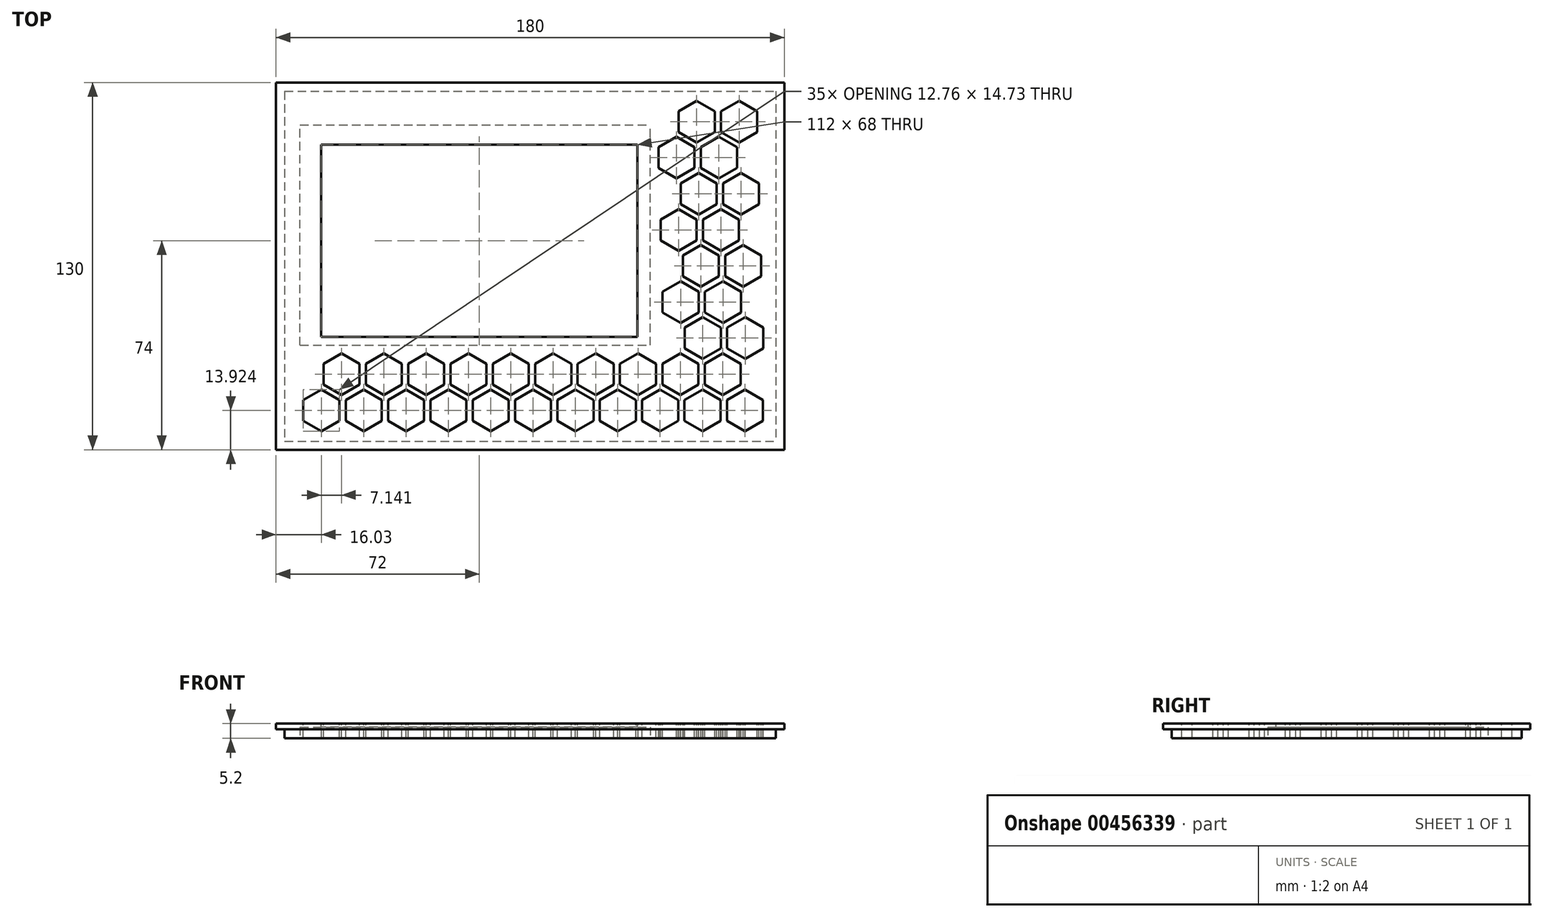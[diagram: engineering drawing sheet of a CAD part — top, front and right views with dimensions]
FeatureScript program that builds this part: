
annotation { "Feature Type Name" : "Feature", "Feature Type Description" : "" }
export const myFeature = defineFeature(function(context is Context, id is Id, definition is map)
    precondition{}
    {
        {
            var Q0;
            Q0=qCreatedBy(makeId("Top.planeOp"),FACE);
            var sketch = newSketch(context, id + "F0", { "sketchPlane" : qUnion([Q0])});
            skLineSegment(sketch, "E0.bottom", {"start": v(42.5, 28) * mm, "end": v(-42.5, 28) * mm});
            skLineSegment(sketch, "E0.top", {"start": v(42.5, -28) * mm, "end": v(-42.5, -28) * mm});
            skLineSegment(sketch, "E0.left", {"start": v(42.5, 28) * mm, "end": v(42.5, -28) * mm});
            skLineSegment(sketch, "E0.right", {"start": v(-42.5, 28) * mm, "end": v(-42.5, -28) * mm});
            skPoint(sketch, "E0.middle", {"position": v(0, 0) * mm});
            skCircle(sketch, "E1", {"center": v(-39, 24.5) * mm, "radius": 1.4 * mm});
            skCircle(sketch, "E2.MirrorC", {"center": v(-34.56, -24.5) * mm, "radius": 1.4 * mm});
            skCircle(sketch, "E3", {"center": v(19, 24.5) * mm, "radius": 1.4 * mm});
            skCircle(sketch, "E4.MirrorC", {"center": v(19, -24.7) * mm, "radius": 1.4 * mm});
            skSolve(sketch);
        }
        {
            var Q0;
            Q0=qCreatedBy(makeId("Top.planeOp"),FACE);
            var sketch = newSketch(context, id + "F1", { "sketchPlane" : qUnion([Q0])});
            skLineSegment(sketch, "E5.bottom", {"start": v(-90, 65) * mm, "end": v(90, 65) * mm});
            skLineSegment(sketch, "E5.top", {"start": v(-90, -65) * mm, "end": v(90, -65) * mm});
            skLineSegment(sketch, "E5.left", {"start": v(-90, 65) * mm, "end": v(-90, -65) * mm});
            skLineSegment(sketch, "E5.right", {"start": v(90, 65) * mm, "end": v(90, -65) * mm});
            skPoint(sketch, "E5.middle", {"position": v(0, 0) * mm});
            skLineSegment(sketch, "E6.bottom", {"start": v(-86.95, 61.95) * mm, "end": v(86.95, 61.95) * mm});
            skLineSegment(sketch, "E6.top", {"start": v(-86.95, -61.95) * mm, "end": v(86.95, -61.95) * mm});
            skLineSegment(sketch, "E6.left", {"start": v(-86.95, 61.95) * mm, "end": v(-86.95, -61.95) * mm});
            skLineSegment(sketch, "E6.right", {"start": v(86.95, 61.95) * mm, "end": v(86.95, -61.95) * mm});
            skSolve(sketch);
        }
        {
            var Q0;
            Q0=qCreatedBy(makeId("Top.planeOp"),FACE);
            var sketch = newSketch(context, id + "F2", { "sketchPlane" : qUnion([Q0])});
            skLineSegment(sketch, "E7.bottom", {"start": v(42.5, 50) * mm, "end": v(-81.5, 50) * mm});
            skLineSegment(sketch, "E7.top", {"start": v(42.5, -28) * mm, "end": v(-81.5, -28) * mm});
            skLineSegment(sketch, "E7.left", {"start": v(42.5, 50) * mm, "end": v(42.5, -28) * mm});
            skLineSegment(sketch, "E7.right", {"start": v(-81.5, 50) * mm, "end": v(-81.5, -28) * mm});
            skPoint(sketch, "E7.middle", {"position": v(0, 0) * mm});
            skSolve(sketch);
        }
        {
            var Q0;
            Q0=makeQuery(id+"F1.imprint","IMPRINT",FACE,{"disambiguationData":[TD([[makeQuery(id+"F1.imprint","IMPRINT",EDGE,{"derivedFrom":sQuery(id+"F1.wireOp",EDGE,"E5.bottom")}),-1.0]])]});
            var Q1;
            Q1=makeQuery(id+"F1.imprint","IMPRINT",FACE,{"disambiguationData":[TD([[makeQuery(id+"F1.imprint","IMPRINT",EDGE,{"derivedFrom":sQuery(id+"F1.wireOp",EDGE,"E6.bottom")}),-1.0]])]});
            extrude(context, id + "F3", {"entities" : qUnion([Q0, Q1]), "depth" : 2 * mm});
        }
        {
            var Q0;
            Q0=makeQuery(id+"F1.imprint","IMPRINT",FACE,{"disambiguationData":[TD([[makeQuery(id+"F1.imprint","IMPRINT",EDGE,{"derivedFrom":sQuery(id+"F1.wireOp",EDGE,"E6.bottom")}),-1.0]])]});
            extrude(context, id + "F4", {"entities" : qUnion([Q0]), "operationType" : NewBodyOperationType.ADD, "oppositeDirection" : true, "depth" : 3.2 * mm});
        }
        {
            var Q0;
            Q0=makeQuery(id+"F2.imprint","IMPRINT",FACE,{"disambiguationData":[TD([[makeQuery(id+"F2.imprint","IMPRINT",EDGE,{"derivedFrom":sQuery(id+"F2.wireOp",EDGE,"E7.bottom")}),1.0]])]});
            extrude(context, id + "F5", {"entities" : qUnion([Q0]), "operationType" : NewBodyOperationType.REMOVE, "endBound" : BoundingType.SYMMETRIC, "depth" : 25 * mm});
        }
        {
            var Q0;
            Q0=makeQuery(id+"F3.opExtrude","CAP_FACE",FACE,{"disambiguationData":[OSD([sQuery(id+"F1.wireOp",EDGE,"E5.bottom"),sQuery(id+"F1.wireOp",EDGE,"E5.top"),sQuery(id+"F1.wireOp",EDGE,"E5.left"),sQuery(id+"F1.wireOp",EDGE,"E5.right")])],"isStart":false});
            var sketch = newSketch(context, id + "F6", { "sketchPlane" : qUnion([Q0])});
            skPoint(sketch, "E8.0.5.0", {"position": v(78.65, 43.94) * mm});
            skCircle(sketch, "E8.0.6.1", {"center": v(73.98, 51.19) * mm, "radius": 6.38 * mm, "construction": true});
            skLineSegment(sketch, "E8.0.6.2", {"start": v(73.98, 43.82) * mm, "end": v(67.6, 47.5) * mm});
            skLineSegment(sketch, "E8.0.6.3", {"start": v(80.36, 47.5) * mm, "end": v(73.98, 43.82) * mm});
            skLineSegment(sketch, "E8.0.6.4", {"start": v(67.6, 54.87) * mm, "end": v(73.98, 58.56) * mm});
            skLineSegment(sketch, "E8.0.6.5", {"start": v(73.98, 58.56) * mm, "end": v(80.36, 54.87) * mm});
            skLineSegment(sketch, "E8.0.6.6", {"start": v(80.36, 54.87) * mm, "end": v(80.36, 47.5) * mm});
            skLineSegment(sketch, "E8.0.6.7", {"start": v(67.6, 47.5) * mm, "end": v(67.6, 54.87) * mm});
            skPoint(sketch, "E8.1.4.0", {"position": v(71.5, 31.16) * mm});
            skCircle(sketch, "E8.1.4.1", {"center": v(74.7, 25.64) * mm, "radius": 6.38 * mm, "construction": true});
            skLineSegment(sketch, "E8.1.4.2", {"start": v(74.7, 18.27) * mm, "end": v(68.32, 21.95) * mm});
            skLineSegment(sketch, "E8.1.4.3", {"start": v(81.08, 21.95) * mm, "end": v(74.7, 18.27) * mm});
            skLineSegment(sketch, "E8.1.4.4", {"start": v(68.32, 29.32) * mm, "end": v(74.7, 33) * mm});
            skLineSegment(sketch, "E8.1.4.5", {"start": v(74.7, 33) * mm, "end": v(81.08, 29.32) * mm});
            skLineSegment(sketch, "E8.1.4.6", {"start": v(81.08, 29.32) * mm, "end": v(81.08, 21.95) * mm});
            skLineSegment(sketch, "E8.1.4.7", {"start": v(68.32, 21.95) * mm, "end": v(68.32, 29.32) * mm});
            skPoint(sketch, "E8.1.5.0", {"position": v(63.65, 43.94) * mm});
            skCircle(sketch, "E8.1.5.1", {"center": v(66.84, 38.41) * mm, "radius": 6.38 * mm, "construction": true});
            skLineSegment(sketch, "E8.1.5.2", {"start": v(66.84, 31.05) * mm, "end": v(60.46, 34.73) * mm});
            skLineSegment(sketch, "E8.1.5.3", {"start": v(73.22, 34.73) * mm, "end": v(66.84, 31.05) * mm});
            skLineSegment(sketch, "E8.1.5.4", {"start": v(60.46, 42.1) * mm, "end": v(66.84, 45.78) * mm});
            skLineSegment(sketch, "E8.1.5.5", {"start": v(66.84, 45.78) * mm, "end": v(73.22, 42.1) * mm});
            skLineSegment(sketch, "E8.1.5.6", {"start": v(73.22, 42.1) * mm, "end": v(73.22, 34.73) * mm});
            skLineSegment(sketch, "E8.1.5.7", {"start": v(60.46, 34.73) * mm, "end": v(60.46, 42.1) * mm});
            skCircle(sketch, "E8.1.6.1", {"center": v(58.98, 51.19) * mm, "radius": 6.38 * mm, "construction": true});
            skLineSegment(sketch, "E8.1.6.2", {"start": v(58.98, 43.82) * mm, "end": v(52.6, 47.5) * mm});
            skLineSegment(sketch, "E8.1.6.3", {"start": v(65.36, 47.5) * mm, "end": v(58.98, 43.82) * mm});
            skLineSegment(sketch, "E8.1.6.4", {"start": v(52.6, 54.87) * mm, "end": v(58.98, 58.56) * mm});
            skLineSegment(sketch, "E8.1.6.5", {"start": v(58.98, 58.56) * mm, "end": v(65.36, 54.87) * mm});
            skLineSegment(sketch, "E8.1.6.6", {"start": v(65.36, 54.87) * mm, "end": v(65.36, 47.5) * mm});
            skLineSegment(sketch, "E8.1.6.7", {"start": v(52.6, 47.5) * mm, "end": v(52.6, 54.87) * mm});
            skPoint(sketch, "E8.2.2.0", {"position": v(72.23, 5.6) * mm});
            skCircle(sketch, "E8.2.2.1", {"center": v(75.42, 0.08) * mm, "radius": 6.38 * mm, "construction": true});
            skLineSegment(sketch, "E8.2.2.2", {"start": v(75.42, -7.28) * mm, "end": v(69.04, -3.6) * mm});
            skLineSegment(sketch, "E8.2.2.3", {"start": v(81.8, -3.6) * mm, "end": v(75.42, -7.28) * mm});
            skLineSegment(sketch, "E8.2.2.4", {"start": v(69.04, 3.77) * mm, "end": v(75.42, 7.45) * mm});
            skLineSegment(sketch, "E8.2.2.5", {"start": v(75.42, 7.45) * mm, "end": v(81.8, 3.77) * mm});
            skLineSegment(sketch, "E8.2.2.6", {"start": v(81.8, 3.77) * mm, "end": v(81.8, -3.6) * mm});
            skLineSegment(sketch, "E8.2.2.7", {"start": v(69.04, -3.6) * mm, "end": v(69.04, 3.77) * mm});
            skPoint(sketch, "E8.2.3.0", {"position": v(64.37, 18.39) * mm});
            skCircle(sketch, "E8.2.3.1", {"center": v(67.56, 12.86) * mm, "radius": 6.38 * mm, "construction": true});
            skLineSegment(sketch, "E8.2.3.2", {"start": v(67.56, 5.5) * mm, "end": v(61.18, 9.18) * mm});
            skLineSegment(sketch, "E8.2.3.3", {"start": v(73.94, 9.18) * mm, "end": v(67.56, 5.5) * mm});
            skLineSegment(sketch, "E8.2.3.4", {"start": v(61.18, 16.54) * mm, "end": v(67.56, 20.23) * mm});
            skLineSegment(sketch, "E8.2.3.5", {"start": v(67.56, 20.23) * mm, "end": v(73.94, 16.54) * mm});
            skLineSegment(sketch, "E8.2.3.6", {"start": v(73.94, 16.54) * mm, "end": v(73.94, 9.18) * mm});
            skLineSegment(sketch, "E8.2.3.7", {"start": v(61.18, 9.18) * mm, "end": v(61.18, 16.54) * mm});
            skPoint(sketch, "E8.2.4.0", {"position": v(56.5, 31.16) * mm});
            skCircle(sketch, "E8.2.4.1", {"center": v(59.7, 25.64) * mm, "radius": 6.38 * mm, "construction": true});
            skLineSegment(sketch, "E8.2.4.2", {"start": v(59.7, 18.27) * mm, "end": v(53.32, 21.95) * mm});
            skLineSegment(sketch, "E8.2.4.3", {"start": v(66.08, 21.95) * mm, "end": v(59.7, 18.27) * mm});
            skLineSegment(sketch, "E8.2.4.4", {"start": v(53.32, 29.32) * mm, "end": v(59.7, 33) * mm});
            skLineSegment(sketch, "E8.2.4.5", {"start": v(59.7, 33) * mm, "end": v(66.08, 29.32) * mm});
            skLineSegment(sketch, "E8.2.4.6", {"start": v(66.08, 29.32) * mm, "end": v(66.08, 21.95) * mm});
            skLineSegment(sketch, "E8.2.4.7", {"start": v(53.32, 21.95) * mm, "end": v(53.32, 29.32) * mm});
            skPoint(sketch, "E8.2.5.0", {"position": v(48.65, 43.94) * mm});
            skCircle(sketch, "E8.2.5.1", {"center": v(51.84, 38.41) * mm, "radius": 6.38 * mm, "construction": true});
            skLineSegment(sketch, "E8.2.5.2", {"start": v(51.84, 31.05) * mm, "end": v(45.46, 34.73) * mm});
            skLineSegment(sketch, "E8.2.5.3", {"start": v(58.22, 34.73) * mm, "end": v(51.84, 31.05) * mm});
            skLineSegment(sketch, "E8.2.5.4", {"start": v(45.46, 42.1) * mm, "end": v(51.84, 45.78) * mm});
            skLineSegment(sketch, "E8.2.5.5", {"start": v(51.84, 45.78) * mm, "end": v(58.22, 42.1) * mm});
            skLineSegment(sketch, "E8.2.5.6", {"start": v(58.22, 42.1) * mm, "end": v(58.22, 34.73) * mm});
            skLineSegment(sketch, "E8.2.5.7", {"start": v(45.46, 34.73) * mm, "end": v(45.46, 42.1) * mm});
            skPoint(sketch, "E8.3.0.0", {"position": v(72.95, -19.94) * mm});
            skCircle(sketch, "E8.3.0.1", {"center": v(76.13, -25.47) * mm, "radius": 6.38 * mm, "construction": true});
            skLineSegment(sketch, "E8.3.0.2", {"start": v(76.13, -32.83) * mm, "end": v(69.76, -29.15) * mm});
            skLineSegment(sketch, "E8.3.0.3", {"start": v(82.51, -29.15) * mm, "end": v(76.13, -32.83) * mm});
            skLineSegment(sketch, "E8.3.0.4", {"start": v(69.76, -21.78) * mm, "end": v(76.13, -18.1) * mm});
            skLineSegment(sketch, "E8.3.0.5", {"start": v(76.13, -18.1) * mm, "end": v(82.51, -21.78) * mm});
            skLineSegment(sketch, "E8.3.0.6", {"start": v(82.51, -21.78) * mm, "end": v(82.51, -29.15) * mm});
            skLineSegment(sketch, "E8.3.0.7", {"start": v(69.76, -29.15) * mm, "end": v(69.76, -21.78) * mm});
            skPoint(sketch, "E8.3.1.0", {"position": v(65.09, -7.17) * mm});
            skCircle(sketch, "E8.3.1.1", {"center": v(68.28, -12.7) * mm, "radius": 6.38 * mm, "construction": true});
            skLineSegment(sketch, "E8.3.1.2", {"start": v(68.28, -20.06) * mm, "end": v(61.9, -16.37) * mm});
            skLineSegment(sketch, "E8.3.1.3", {"start": v(74.65, -16.37) * mm, "end": v(68.28, -20.06) * mm});
            skLineSegment(sketch, "E8.3.1.4", {"start": v(61.9, -9) * mm, "end": v(68.28, -5.33) * mm});
            skLineSegment(sketch, "E8.3.1.5", {"start": v(68.28, -5.33) * mm, "end": v(74.65, -9) * mm});
            skLineSegment(sketch, "E8.3.1.6", {"start": v(74.65, -9) * mm, "end": v(74.65, -16.37) * mm});
            skLineSegment(sketch, "E8.3.1.7", {"start": v(61.9, -16.37) * mm, "end": v(61.9, -9) * mm});
            skPoint(sketch, "E8.3.2.0", {"position": v(57.23, 5.6) * mm});
            skCircle(sketch, "E8.3.2.1", {"center": v(60.42, 0.08) * mm, "radius": 6.38 * mm, "construction": true});
            skLineSegment(sketch, "E8.3.2.2", {"start": v(60.42, -7.28) * mm, "end": v(54.04, -3.6) * mm});
            skLineSegment(sketch, "E8.3.2.3", {"start": v(66.8, -3.6) * mm, "end": v(60.42, -7.28) * mm});
            skLineSegment(sketch, "E8.3.2.4", {"start": v(54.04, 3.77) * mm, "end": v(60.42, 7.45) * mm});
            skLineSegment(sketch, "E8.3.2.5", {"start": v(60.42, 7.45) * mm, "end": v(66.8, 3.77) * mm});
            skLineSegment(sketch, "E8.3.2.6", {"start": v(66.8, 3.77) * mm, "end": v(66.8, -3.6) * mm});
            skLineSegment(sketch, "E8.3.2.7", {"start": v(54.04, -3.6) * mm, "end": v(54.04, 3.77) * mm});
            skPoint(sketch, "E8.3.3.0", {"position": v(49.37, 18.39) * mm});
            skCircle(sketch, "E8.3.3.1", {"center": v(52.56, 12.86) * mm, "radius": 6.38 * mm, "construction": true});
            skLineSegment(sketch, "E8.3.3.2", {"start": v(52.56, 5.5) * mm, "end": v(46.18, 9.18) * mm});
            skLineSegment(sketch, "E8.3.3.3", {"start": v(58.94, 9.18) * mm, "end": v(52.56, 5.5) * mm});
            skLineSegment(sketch, "E8.3.3.4", {"start": v(46.18, 16.54) * mm, "end": v(52.56, 20.23) * mm});
            skLineSegment(sketch, "E8.3.3.5", {"start": v(52.56, 20.23) * mm, "end": v(58.94, 16.54) * mm});
            skLineSegment(sketch, "E8.3.3.6", {"start": v(58.94, 16.54) * mm, "end": v(58.94, 9.18) * mm});
            skLineSegment(sketch, "E8.3.3.7", {"start": v(46.18, 9.18) * mm, "end": v(46.18, 16.54) * mm});
            skPoint(sketch, "E8.4.0.0", {"position": v(57.95, -19.94) * mm});
            skCircle(sketch, "E8.4.0.1", {"center": v(61.13, -25.47) * mm, "radius": 6.38 * mm, "construction": true});
            skLineSegment(sketch, "E8.4.0.2", {"start": v(61.13, -32.83) * mm, "end": v(54.76, -29.15) * mm});
            skLineSegment(sketch, "E8.4.0.3", {"start": v(67.51, -29.15) * mm, "end": v(61.13, -32.83) * mm});
            skLineSegment(sketch, "E8.4.0.4", {"start": v(54.76, -21.78) * mm, "end": v(61.13, -18.1) * mm});
            skLineSegment(sketch, "E8.4.0.5", {"start": v(61.13, -18.1) * mm, "end": v(67.51, -21.78) * mm});
            skLineSegment(sketch, "E8.4.0.6", {"start": v(67.51, -21.78) * mm, "end": v(67.51, -29.15) * mm});
            skLineSegment(sketch, "E8.4.0.7", {"start": v(54.76, -29.15) * mm, "end": v(54.76, -21.78) * mm});
            skPoint(sketch, "E8.4.1.0", {"position": v(50.09, -7.17) * mm});
            skCircle(sketch, "E8.4.1.1", {"center": v(53.28, -12.7) * mm, "radius": 6.38 * mm, "construction": true});
            skLineSegment(sketch, "E8.4.1.2", {"start": v(53.28, -20.06) * mm, "end": v(46.9, -16.37) * mm});
            skLineSegment(sketch, "E8.4.1.3", {"start": v(59.65, -16.37) * mm, "end": v(53.28, -20.06) * mm});
            skLineSegment(sketch, "E8.4.1.4", {"start": v(46.9, -9) * mm, "end": v(53.28, -5.33) * mm});
            skLineSegment(sketch, "E8.4.1.5", {"start": v(53.28, -5.33) * mm, "end": v(59.65, -9) * mm});
            skLineSegment(sketch, "E8.4.1.6", {"start": v(59.65, -9) * mm, "end": v(59.65, -16.37) * mm});
            skLineSegment(sketch, "E8.4.1.7", {"start": v(46.9, -16.37) * mm, "end": v(46.9, -9) * mm});
            skPoint(sketch, "E9.3.0.0", {"position": v(72.84, -45.55) * mm});
            skCircle(sketch, "E9.3.0.1", {"center": v(76.03, -51.08) * mm, "radius": 6.38 * mm, "construction": true});
            skLineSegment(sketch, "E9.3.0.2", {"start": v(76.03, -58.44) * mm, "end": v(69.65, -54.76) * mm});
            skLineSegment(sketch, "E9.3.0.3", {"start": v(82.4, -54.76) * mm, "end": v(76.03, -58.44) * mm});
            skLineSegment(sketch, "E9.3.0.4", {"start": v(69.65, -47.4) * mm, "end": v(76.03, -43.71) * mm});
            skLineSegment(sketch, "E9.3.0.5", {"start": v(76.03, -43.71) * mm, "end": v(82.4, -47.4) * mm});
            skLineSegment(sketch, "E9.3.0.6", {"start": v(82.4, -47.4) * mm, "end": v(82.4, -54.76) * mm});
            skLineSegment(sketch, "E9.3.0.7", {"start": v(69.65, -54.76) * mm, "end": v(69.65, -47.4) * mm});
            skPoint(sketch, "E9.3.1.0", {"position": v(64.98, -32.78) * mm});
            skCircle(sketch, "E9.3.1.1", {"center": v(68.17, -38.3) * mm, "radius": 6.38 * mm, "construction": true});
            skLineSegment(sketch, "E9.3.1.2", {"start": v(68.17, -45.67) * mm, "end": v(61.8, -41.98) * mm});
            skLineSegment(sketch, "E9.3.1.3", {"start": v(74.55, -41.98) * mm, "end": v(68.17, -45.67) * mm});
            skLineSegment(sketch, "E9.3.1.4", {"start": v(61.8, -34.62) * mm, "end": v(68.17, -30.93) * mm});
            skLineSegment(sketch, "E9.3.1.5", {"start": v(68.17, -30.93) * mm, "end": v(74.55, -34.62) * mm});
            skLineSegment(sketch, "E9.3.1.6", {"start": v(74.55, -34.62) * mm, "end": v(74.55, -41.98) * mm});
            skLineSegment(sketch, "E9.3.1.7", {"start": v(61.8, -41.98) * mm, "end": v(61.8, -34.62) * mm});
            skPoint(sketch, "E9.4.0.0", {"position": v(57.84, -45.55) * mm});
            skCircle(sketch, "E9.4.0.1", {"center": v(61.03, -51.08) * mm, "radius": 6.38 * mm, "construction": true});
            skLineSegment(sketch, "E9.4.0.2", {"start": v(61.03, -58.44) * mm, "end": v(54.65, -54.76) * mm});
            skLineSegment(sketch, "E9.4.0.3", {"start": v(67.4, -54.76) * mm, "end": v(61.03, -58.44) * mm});
            skLineSegment(sketch, "E9.4.0.4", {"start": v(54.65, -47.4) * mm, "end": v(61.03, -43.71) * mm});
            skLineSegment(sketch, "E9.4.0.5", {"start": v(61.03, -43.71) * mm, "end": v(67.4, -47.4) * mm});
            skLineSegment(sketch, "E9.4.0.6", {"start": v(67.4, -47.4) * mm, "end": v(67.4, -54.76) * mm});
            skLineSegment(sketch, "E9.4.0.7", {"start": v(54.65, -54.76) * mm, "end": v(54.65, -47.4) * mm});
            skPoint(sketch, "E9.4.1.0", {"position": v(49.98, -32.78) * mm});
            skCircle(sketch, "E9.4.1.1", {"center": v(53.17, -38.3) * mm, "radius": 6.38 * mm, "construction": true});
            skLineSegment(sketch, "E9.4.1.2", {"start": v(53.17, -45.67) * mm, "end": v(46.8, -41.98) * mm});
            skLineSegment(sketch, "E9.4.1.3", {"start": v(59.55, -41.98) * mm, "end": v(53.17, -45.67) * mm});
            skLineSegment(sketch, "E9.4.1.4", {"start": v(46.8, -34.62) * mm, "end": v(53.17, -30.93) * mm});
            skLineSegment(sketch, "E9.4.1.5", {"start": v(53.17, -30.93) * mm, "end": v(59.55, -34.62) * mm});
            skLineSegment(sketch, "E9.4.1.6", {"start": v(59.55, -34.62) * mm, "end": v(59.55, -41.98) * mm});
            skLineSegment(sketch, "E9.4.1.7", {"start": v(46.8, -41.98) * mm, "end": v(46.8, -34.62) * mm});
            skPoint(sketch, "E9.5.0.0", {"position": v(42.84, -45.55) * mm});
            skCircle(sketch, "E9.5.0.1", {"center": v(46.03, -51.08) * mm, "radius": 6.38 * mm, "construction": true});
            skLineSegment(sketch, "E9.5.0.2", {"start": v(46.03, -58.44) * mm, "end": v(39.65, -54.76) * mm});
            skLineSegment(sketch, "E9.5.0.3", {"start": v(52.4, -54.76) * mm, "end": v(46.03, -58.44) * mm});
            skLineSegment(sketch, "E9.5.0.4", {"start": v(39.65, -47.4) * mm, "end": v(46.03, -43.71) * mm});
            skLineSegment(sketch, "E9.5.0.5", {"start": v(46.03, -43.71) * mm, "end": v(52.4, -47.4) * mm});
            skLineSegment(sketch, "E9.5.0.6", {"start": v(52.4, -47.4) * mm, "end": v(52.4, -54.76) * mm});
            skLineSegment(sketch, "E9.5.0.7", {"start": v(39.65, -54.76) * mm, "end": v(39.65, -47.4) * mm});
            skPoint(sketch, "E9.5.1.0", {"position": v(34.98, -32.78) * mm});
            skCircle(sketch, "E9.5.1.1", {"center": v(38.17, -38.3) * mm, "radius": 6.38 * mm, "construction": true});
            skLineSegment(sketch, "E9.5.1.2", {"start": v(38.17, -45.67) * mm, "end": v(31.8, -41.98) * mm});
            skLineSegment(sketch, "E9.5.1.3", {"start": v(44.55, -41.98) * mm, "end": v(38.17, -45.67) * mm});
            skLineSegment(sketch, "E9.5.1.4", {"start": v(31.8, -34.62) * mm, "end": v(38.17, -30.93) * mm});
            skLineSegment(sketch, "E9.5.1.5", {"start": v(38.17, -30.93) * mm, "end": v(44.55, -34.62) * mm});
            skLineSegment(sketch, "E9.5.1.6", {"start": v(44.55, -34.62) * mm, "end": v(44.55, -41.98) * mm});
            skLineSegment(sketch, "E9.5.1.7", {"start": v(31.8, -41.98) * mm, "end": v(31.8, -34.62) * mm});
            skPoint(sketch, "E9.6.0.0", {"position": v(27.84, -45.55) * mm});
            skCircle(sketch, "E9.6.0.1", {"center": v(31.03, -51.08) * mm, "radius": 6.38 * mm, "construction": true});
            skLineSegment(sketch, "E9.6.0.2", {"start": v(31.03, -58.44) * mm, "end": v(24.65, -54.76) * mm});
            skLineSegment(sketch, "E9.6.0.3", {"start": v(37.4, -54.76) * mm, "end": v(31.03, -58.44) * mm});
            skLineSegment(sketch, "E9.6.0.4", {"start": v(24.65, -47.4) * mm, "end": v(31.03, -43.71) * mm});
            skLineSegment(sketch, "E9.6.0.5", {"start": v(31.03, -43.71) * mm, "end": v(37.4, -47.4) * mm});
            skLineSegment(sketch, "E9.6.0.6", {"start": v(37.4, -47.4) * mm, "end": v(37.4, -54.76) * mm});
            skLineSegment(sketch, "E9.6.0.7", {"start": v(24.65, -54.76) * mm, "end": v(24.65, -47.4) * mm});
            skPoint(sketch, "E9.6.1.0", {"position": v(19.98, -32.78) * mm});
            skCircle(sketch, "E9.6.1.1", {"center": v(23.17, -38.3) * mm, "radius": 6.38 * mm, "construction": true});
            skLineSegment(sketch, "E9.6.1.2", {"start": v(23.17, -45.67) * mm, "end": v(16.8, -41.98) * mm});
            skLineSegment(sketch, "E9.6.1.3", {"start": v(29.55, -41.98) * mm, "end": v(23.17, -45.67) * mm});
            skLineSegment(sketch, "E9.6.1.4", {"start": v(16.8, -34.62) * mm, "end": v(23.17, -30.93) * mm});
            skLineSegment(sketch, "E9.6.1.5", {"start": v(23.17, -30.93) * mm, "end": v(29.55, -34.62) * mm});
            skLineSegment(sketch, "E9.6.1.6", {"start": v(29.55, -34.62) * mm, "end": v(29.55, -41.98) * mm});
            skLineSegment(sketch, "E9.6.1.7", {"start": v(16.8, -41.98) * mm, "end": v(16.8, -34.62) * mm});
            skPoint(sketch, "E9.7.0.0", {"position": v(12.84, -45.55) * mm});
            skCircle(sketch, "E9.7.0.1", {"center": v(16.03, -51.08) * mm, "radius": 6.38 * mm, "construction": true});
            skLineSegment(sketch, "E9.7.0.2", {"start": v(16.03, -58.44) * mm, "end": v(9.65, -54.76) * mm});
            skLineSegment(sketch, "E9.7.0.3", {"start": v(22.4, -54.76) * mm, "end": v(16.03, -58.44) * mm});
            skLineSegment(sketch, "E9.7.0.4", {"start": v(9.65, -47.4) * mm, "end": v(16.03, -43.71) * mm});
            skLineSegment(sketch, "E9.7.0.5", {"start": v(16.03, -43.71) * mm, "end": v(22.4, -47.4) * mm});
            skLineSegment(sketch, "E9.7.0.6", {"start": v(22.4, -47.4) * mm, "end": v(22.4, -54.76) * mm});
            skLineSegment(sketch, "E9.7.0.7", {"start": v(9.65, -54.76) * mm, "end": v(9.65, -47.4) * mm});
            skPoint(sketch, "E9.7.1.0", {"position": v(4.98, -32.78) * mm});
            skCircle(sketch, "E9.7.1.1", {"center": v(8.17, -38.3) * mm, "radius": 6.38 * mm, "construction": true});
            skLineSegment(sketch, "E9.7.1.2", {"start": v(8.17, -45.67) * mm, "end": v(1.8, -41.98) * mm});
            skLineSegment(sketch, "E9.7.1.3", {"start": v(14.55, -41.98) * mm, "end": v(8.17, -45.67) * mm});
            skLineSegment(sketch, "E9.7.1.4", {"start": v(1.8, -34.62) * mm, "end": v(8.17, -30.93) * mm});
            skLineSegment(sketch, "E9.7.1.5", {"start": v(8.17, -30.93) * mm, "end": v(14.55, -34.62) * mm});
            skLineSegment(sketch, "E9.7.1.6", {"start": v(14.55, -34.62) * mm, "end": v(14.55, -41.98) * mm});
            skLineSegment(sketch, "E9.7.1.7", {"start": v(1.8, -41.98) * mm, "end": v(1.8, -34.62) * mm});
            skPoint(sketch, "E9.8.0.0", {"position": v(-2.16, -45.55) * mm});
            skCircle(sketch, "E9.8.0.1", {"center": v(1.03, -51.08) * mm, "radius": 6.38 * mm, "construction": true});
            skLineSegment(sketch, "E9.8.0.2", {"start": v(1.03, -58.44) * mm, "end": v(-5.35, -54.76) * mm});
            skLineSegment(sketch, "E9.8.0.3", {"start": v(7.4, -54.76) * mm, "end": v(1.03, -58.44) * mm});
            skLineSegment(sketch, "E9.8.0.4", {"start": v(-5.35, -47.4) * mm, "end": v(1.03, -43.71) * mm});
            skLineSegment(sketch, "E9.8.0.5", {"start": v(1.03, -43.71) * mm, "end": v(7.4, -47.4) * mm});
            skLineSegment(sketch, "E9.8.0.6", {"start": v(7.4, -47.4) * mm, "end": v(7.4, -54.76) * mm});
            skLineSegment(sketch, "E9.8.0.7", {"start": v(-5.35, -54.76) * mm, "end": v(-5.35, -47.4) * mm});
            skPoint(sketch, "E9.8.1.0", {"position": v(-10.02, -32.78) * mm});
            skCircle(sketch, "E9.8.1.1", {"center": v(-6.83, -38.3) * mm, "radius": 6.38 * mm, "construction": true});
            skLineSegment(sketch, "E9.8.1.2", {"start": v(-6.83, -45.67) * mm, "end": v(-13.2, -41.98) * mm});
            skLineSegment(sketch, "E9.8.1.3", {"start": v(-0.45, -41.98) * mm, "end": v(-6.83, -45.67) * mm});
            skLineSegment(sketch, "E9.8.1.4", {"start": v(-13.2, -34.62) * mm, "end": v(-6.83, -30.93) * mm});
            skLineSegment(sketch, "E9.8.1.5", {"start": v(-6.83, -30.93) * mm, "end": v(-0.45, -34.62) * mm});
            skLineSegment(sketch, "E9.8.1.6", {"start": v(-0.45, -34.62) * mm, "end": v(-0.45, -41.98) * mm});
            skLineSegment(sketch, "E9.8.1.7", {"start": v(-13.2, -41.98) * mm, "end": v(-13.2, -34.62) * mm});
            skPoint(sketch, "E9.9.0.0", {"position": v(-17.16, -45.55) * mm});
            skCircle(sketch, "E9.9.0.1", {"center": v(-13.97, -51.08) * mm, "radius": 6.38 * mm, "construction": true});
            skLineSegment(sketch, "E9.9.0.2", {"start": v(-13.97, -58.44) * mm, "end": v(-20.35, -54.76) * mm});
            skLineSegment(sketch, "E9.9.0.3", {"start": v(-7.6, -54.76) * mm, "end": v(-13.97, -58.44) * mm});
            skLineSegment(sketch, "E9.9.0.4", {"start": v(-20.35, -47.4) * mm, "end": v(-13.97, -43.71) * mm});
            skLineSegment(sketch, "E9.9.0.5", {"start": v(-13.97, -43.71) * mm, "end": v(-7.6, -47.4) * mm});
            skLineSegment(sketch, "E9.9.0.6", {"start": v(-7.6, -47.4) * mm, "end": v(-7.6, -54.76) * mm});
            skLineSegment(sketch, "E9.9.0.7", {"start": v(-20.35, -54.76) * mm, "end": v(-20.35, -47.4) * mm});
            skPoint(sketch, "E9.9.1.0", {"position": v(-25.02, -32.78) * mm});
            skCircle(sketch, "E9.9.1.1", {"center": v(-21.83, -38.3) * mm, "radius": 6.38 * mm, "construction": true});
            skLineSegment(sketch, "E9.9.1.2", {"start": v(-21.83, -45.67) * mm, "end": v(-28.2, -41.98) * mm});
            skLineSegment(sketch, "E9.9.1.3", {"start": v(-15.45, -41.98) * mm, "end": v(-21.83, -45.67) * mm});
            skLineSegment(sketch, "E9.9.1.4", {"start": v(-28.2, -34.62) * mm, "end": v(-21.83, -30.93) * mm});
            skLineSegment(sketch, "E9.9.1.5", {"start": v(-21.83, -30.93) * mm, "end": v(-15.45, -34.62) * mm});
            skLineSegment(sketch, "E9.9.1.6", {"start": v(-15.45, -34.62) * mm, "end": v(-15.45, -41.98) * mm});
            skLineSegment(sketch, "E9.9.1.7", {"start": v(-28.2, -41.98) * mm, "end": v(-28.2, -34.62) * mm});
            skPoint(sketch, "E9.10.0.0", {"position": v(-32.16, -45.55) * mm});
            skCircle(sketch, "E9.10.0.1", {"center": v(-28.97, -51.08) * mm, "radius": 6.38 * mm, "construction": true});
            skLineSegment(sketch, "E9.10.0.2", {"start": v(-28.97, -58.44) * mm, "end": v(-35.35, -54.76) * mm});
            skLineSegment(sketch, "E9.10.0.3", {"start": v(-22.6, -54.76) * mm, "end": v(-28.97, -58.44) * mm});
            skLineSegment(sketch, "E9.10.0.4", {"start": v(-35.35, -47.4) * mm, "end": v(-28.97, -43.71) * mm});
            skLineSegment(sketch, "E9.10.0.5", {"start": v(-28.97, -43.71) * mm, "end": v(-22.6, -47.4) * mm});
            skLineSegment(sketch, "E9.10.0.6", {"start": v(-22.6, -47.4) * mm, "end": v(-22.6, -54.76) * mm});
            skLineSegment(sketch, "E9.10.0.7", {"start": v(-35.35, -54.76) * mm, "end": v(-35.35, -47.4) * mm});
            skPoint(sketch, "E9.10.1.0", {"position": v(-40.02, -32.78) * mm});
            skCircle(sketch, "E9.10.1.1", {"center": v(-36.83, -38.3) * mm, "radius": 6.38 * mm, "construction": true});
            skLineSegment(sketch, "E9.10.1.2", {"start": v(-36.83, -45.67) * mm, "end": v(-43.2, -41.98) * mm});
            skLineSegment(sketch, "E9.10.1.3", {"start": v(-30.45, -41.98) * mm, "end": v(-36.83, -45.67) * mm});
            skLineSegment(sketch, "E9.10.1.4", {"start": v(-43.2, -34.62) * mm, "end": v(-36.83, -30.93) * mm});
            skLineSegment(sketch, "E9.10.1.5", {"start": v(-36.83, -30.93) * mm, "end": v(-30.45, -34.62) * mm});
            skLineSegment(sketch, "E9.10.1.6", {"start": v(-30.45, -34.62) * mm, "end": v(-30.45, -41.98) * mm});
            skLineSegment(sketch, "E9.10.1.7", {"start": v(-43.2, -41.98) * mm, "end": v(-43.2, -34.62) * mm});
            skPoint(sketch, "E9.11.0.0", {"position": v(-47.16, -45.55) * mm});
            skCircle(sketch, "E9.11.0.1", {"center": v(-43.97, -51.08) * mm, "radius": 6.38 * mm, "construction": true});
            skLineSegment(sketch, "E9.11.0.2", {"start": v(-43.97, -58.44) * mm, "end": v(-50.35, -54.76) * mm});
            skLineSegment(sketch, "E9.11.0.3", {"start": v(-37.6, -54.76) * mm, "end": v(-43.97, -58.44) * mm});
            skLineSegment(sketch, "E9.11.0.4", {"start": v(-50.35, -47.4) * mm, "end": v(-43.97, -43.71) * mm});
            skLineSegment(sketch, "E9.11.0.5", {"start": v(-43.97, -43.71) * mm, "end": v(-37.6, -47.4) * mm});
            skLineSegment(sketch, "E9.11.0.6", {"start": v(-37.6, -47.4) * mm, "end": v(-37.6, -54.76) * mm});
            skLineSegment(sketch, "E9.11.0.7", {"start": v(-50.35, -54.76) * mm, "end": v(-50.35, -47.4) * mm});
            skPoint(sketch, "E9.11.1.0", {"position": v(-55.02, -32.78) * mm});
            skCircle(sketch, "E9.11.1.1", {"center": v(-51.83, -38.3) * mm, "radius": 6.38 * mm, "construction": true});
            skLineSegment(sketch, "E9.11.1.2", {"start": v(-51.83, -45.67) * mm, "end": v(-58.2, -41.98) * mm});
            skLineSegment(sketch, "E9.11.1.3", {"start": v(-45.45, -41.98) * mm, "end": v(-51.83, -45.67) * mm});
            skLineSegment(sketch, "E9.11.1.4", {"start": v(-58.2, -34.62) * mm, "end": v(-51.83, -30.93) * mm});
            skLineSegment(sketch, "E9.11.1.5", {"start": v(-51.83, -30.93) * mm, "end": v(-45.45, -34.62) * mm});
            skLineSegment(sketch, "E9.11.1.6", {"start": v(-45.45, -34.62) * mm, "end": v(-45.45, -41.98) * mm});
            skLineSegment(sketch, "E9.11.1.7", {"start": v(-58.2, -41.98) * mm, "end": v(-58.2, -34.62) * mm});
            skPoint(sketch, "E9.12.0.0", {"position": v(-62.16, -45.55) * mm});
            skCircle(sketch, "E9.12.0.1", {"center": v(-58.97, -51.08) * mm, "radius": 6.38 * mm, "construction": true});
            skLineSegment(sketch, "E9.12.0.2", {"start": v(-58.97, -58.44) * mm, "end": v(-65.35, -54.76) * mm});
            skLineSegment(sketch, "E9.12.0.3", {"start": v(-52.6, -54.76) * mm, "end": v(-58.97, -58.44) * mm});
            skLineSegment(sketch, "E9.12.0.4", {"start": v(-65.35, -47.4) * mm, "end": v(-58.97, -43.71) * mm});
            skLineSegment(sketch, "E9.12.0.5", {"start": v(-58.97, -43.71) * mm, "end": v(-52.6, -47.4) * mm});
            skLineSegment(sketch, "E9.12.0.6", {"start": v(-52.6, -47.4) * mm, "end": v(-52.6, -54.76) * mm});
            skLineSegment(sketch, "E9.12.0.7", {"start": v(-65.35, -54.76) * mm, "end": v(-65.35, -47.4) * mm});
            skPoint(sketch, "E9.12.1.0", {"position": v(-70.02, -32.78) * mm});
            skCircle(sketch, "E9.12.1.1", {"center": v(-66.83, -38.3) * mm, "radius": 6.38 * mm, "construction": true});
            skLineSegment(sketch, "E9.12.1.2", {"start": v(-66.83, -45.67) * mm, "end": v(-73.2, -41.98) * mm});
            skLineSegment(sketch, "E9.12.1.3", {"start": v(-60.45, -41.98) * mm, "end": v(-66.83, -45.67) * mm});
            skLineSegment(sketch, "E9.12.1.4", {"start": v(-73.2, -34.62) * mm, "end": v(-66.83, -30.93) * mm});
            skLineSegment(sketch, "E9.12.1.5", {"start": v(-66.83, -30.93) * mm, "end": v(-60.45, -34.62) * mm});
            skLineSegment(sketch, "E9.12.1.6", {"start": v(-60.45, -34.62) * mm, "end": v(-60.45, -41.98) * mm});
            skLineSegment(sketch, "E9.12.1.7", {"start": v(-73.2, -41.98) * mm, "end": v(-73.2, -34.62) * mm});
            skPoint(sketch, "E9.13.0.0", {"position": v(-77.16, -45.55) * mm});
            skCircle(sketch, "E9.13.0.1", {"center": v(-73.97, -51.08) * mm, "radius": 6.38 * mm, "construction": true});
            skLineSegment(sketch, "E9.13.0.2", {"start": v(-73.97, -58.44) * mm, "end": v(-80.35, -54.76) * mm});
            skLineSegment(sketch, "E9.13.0.3", {"start": v(-67.6, -54.76) * mm, "end": v(-73.97, -58.44) * mm});
            skLineSegment(sketch, "E9.13.0.4", {"start": v(-80.35, -47.4) * mm, "end": v(-73.97, -43.71) * mm});
            skLineSegment(sketch, "E9.13.0.5", {"start": v(-73.97, -43.71) * mm, "end": v(-67.6, -47.4) * mm});
            skLineSegment(sketch, "E9.13.0.6", {"start": v(-67.6, -47.4) * mm, "end": v(-67.6, -54.76) * mm});
            skLineSegment(sketch, "E9.13.0.7", {"start": v(-80.35, -54.76) * mm, "end": v(-80.35, -47.4) * mm});
            skSolve(sketch);
        }
        {
            var Q0;
            Q0=qSketchRegion(id+"F6",true);
            extrude(context, id + "F7", {"entities" : qUnion([Q0]), "operationType" : NewBodyOperationType.REMOVE, "endBound" : BoundingType.THROUGH_ALL, "oppositeDirection" : true, "depth" : 25 * mm});
        }
        {
            var Q0;
            Q0=makeQuery(id+"F3.opExtrude","CAP_FACE",FACE,{"disambiguationData":[OSD([sQuery(id+"F1.wireOp",EDGE,"E5.bottom"),sQuery(id+"F1.wireOp",EDGE,"E5.top"),sQuery(id+"F1.wireOp",EDGE,"E5.left"),sQuery(id+"F1.wireOp",EDGE,"E5.right")])],"isStart":false});
            var sketch = newSketch(context, id + "F8", { "sketchPlane" : qUnion([Q0])});
            skLineSegment(sketch, "E10.bottom", {"start": v(38, -25) * mm, "end": v(-74, -25) * mm});
            skLineSegment(sketch, "E10.top", {"start": v(38, 43) * mm, "end": v(-74, 43) * mm});
            skLineSegment(sketch, "E10.left", {"start": v(38, -25) * mm, "end": v(38, 43) * mm});
            skLineSegment(sketch, "E10.right", {"start": v(-74, -25) * mm, "end": v(-74, 43) * mm});
            skLineSegment(sketch, "E11.0", {"start": v(42.5, -28) * mm, "end": v(-81.5, -28) * mm});
            skLineSegment(sketch, "E12.0", {"start": v(42.5, 50) * mm, "end": v(42.5, -28) * mm});
            skLineSegment(sketch, "E13.0", {"start": v(-81.5, 50) * mm, "end": v(-81.5, -28) * mm});
            skLineSegment(sketch, "E14.0", {"start": v(42.5, 50) * mm, "end": v(-81.5, 50) * mm});
            skSolve(sketch);
        }
        {
            var Q0;
            Q0=qSketchRegion(id+"F8",true);
            extrude(context, id + "F9", {"entities" : qUnion([Q0]), "operationType" : NewBodyOperationType.ADD, "oppositeDirection" : true, "depth" : 1.2 * mm});
        }
    });
